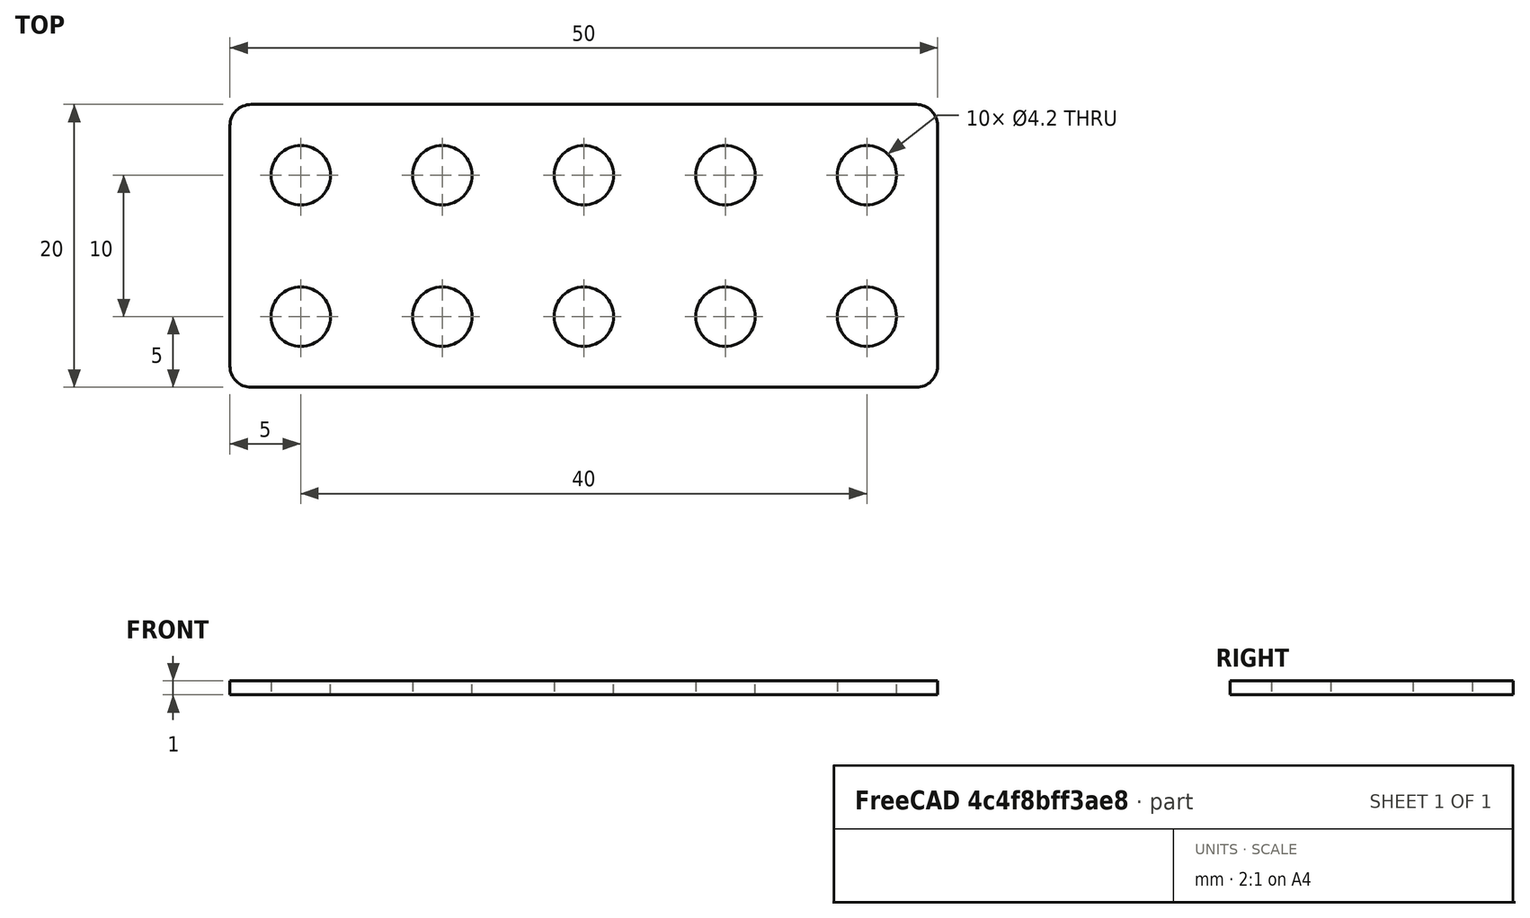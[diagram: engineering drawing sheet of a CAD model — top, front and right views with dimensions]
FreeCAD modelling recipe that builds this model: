
FCSTD DOCUMENT  (FreeCAD 0.16RUnknown)
Label: strip_2x5
License: All rights reserved
LicenseURL: http://en.wikipedia.org/wiki/All_rights_reserved
objects: Sketcher::SketchObject×1, PartDesign::Pad×1
note: 3 computed .brp shape members not serialized (recipe doc carries the construction recipe); baked Part::Feature solids carry a one-line shape summary decoded from their .brp

FEATURE [Sketcher::SketchObject] Sketch
  sketch-geometry (26):
    g0: LineSegment StartX=-3.5 StartY=15 StartZ=0 EndX=43.5 EndY=15 EndZ=0
    g1: LineSegment StartX=45 StartY=13.5 StartZ=0 EndX=45 EndY=-3.5 EndZ=0
    g2: LineSegment StartX=43.5 StartY=-5 StartZ=0 EndX=-3.5 EndY=-5 EndZ=0
    g3: LineSegment StartX=-5 StartY=-3.5 StartZ=0 EndX=-5 EndY=13.5 EndZ=0
    g4: ArcOfCircle CenterX=43.5 CenterY=13.5 CenterZ=0 NormalX=0 NormalY=0 NormalZ=1 Radius=1.5 StartAngle=0 EndAngle=1.5708
    g5: ArcOfCircle CenterX=43.5 CenterY=-3.5 CenterZ=0 NormalX=0 NormalY=0 NormalZ=1 Radius=1.5 StartAngle=4.71239 EndAngle=6.28319
    g6: ArcOfCircle CenterX=-3.5 CenterY=-3.5 CenterZ=0 NormalX=0 NormalY=0 NormalZ=1 Radius=1.5 StartAngle=3.14159 EndAngle=4.71239
    g7: ArcOfCircle CenterX=-3.5 CenterY=13.5 CenterZ=0 NormalX=0 NormalY=0 NormalZ=1 Radius=1.5 StartAngle=1.5708 EndAngle=3.14159
    g8: Circle CenterX=0 CenterY=0 CenterZ=0 NormalX=0 NormalY=0 NormalZ=1 Radius=2.1
    g9: Circle CenterX=0 CenterY=10 CenterZ=0 NormalX=0 NormalY=0 NormalZ=1 Radius=2.1
    g10: Circle CenterX=10 CenterY=0 CenterZ=0 NormalX=0 NormalY=0 NormalZ=1 Radius=2.1
    g11: LineSegment [constr] StartX=0 StartY=0 StartZ=0 EndX=10 EndY=0 EndZ=0
    g12: Circle CenterX=20 CenterY=0 CenterZ=0 NormalX=0 NormalY=0 NormalZ=1 Radius=2.1
    g13: LineSegment [constr] StartX=10 StartY=0 StartZ=0 EndX=20 EndY=0 EndZ=0
    g14: Circle CenterX=30 CenterY=0 CenterZ=0 NormalX=0 NormalY=0 NormalZ=1 Radius=2.1
    g15: LineSegment [constr] StartX=20 StartY=0 StartZ=0 EndX=30 EndY=0 EndZ=0
    g16: Circle CenterX=40 CenterY=0 CenterZ=0 NormalX=0 NormalY=0 NormalZ=1 Radius=2.1
    g17: LineSegment [constr] StartX=30 StartY=0 StartZ=0 EndX=40 EndY=0 EndZ=0
    g18: Circle CenterX=10 CenterY=10 CenterZ=0 NormalX=0 NormalY=0 NormalZ=1 Radius=2.1
    g19: LineSegment [constr] StartX=0 StartY=10 StartZ=0 EndX=10 EndY=10 EndZ=0
    g20: Circle CenterX=20 CenterY=10 CenterZ=0 NormalX=0 NormalY=0 NormalZ=1 Radius=2.1
    g21: LineSegment [constr] StartX=10 StartY=10 StartZ=0 EndX=20 EndY=10 EndZ=0
    g22: Circle CenterX=30 CenterY=10 CenterZ=0 NormalX=0 NormalY=0 NormalZ=1 Radius=2.1
    g23: LineSegment [constr] StartX=20 StartY=10 StartZ=0 EndX=30 EndY=10 EndZ=0
    g24: Circle CenterX=40 CenterY=10 CenterZ=0 NormalX=0 NormalY=0 NormalZ=1 Radius=2.1
    g25: LineSegment [constr] StartX=30 StartY=10 StartZ=0 EndX=40 EndY=10 EndZ=0
  constraints (65):
    c: Horizontal(g0)
    c: Horizontal(g2)
    c: Vertical(g1)
    c: Vertical(g3)
    c: Tangent(g0,g4) = 1.5708
    c: Tangent(g1,g4) = 1.5708
    c: Tangent(g1,g5) = 1.5708
    c: Tangent(g2,g5) = 1.5708
    c: Tangent(g3,g6) = 1.5708
    c: Tangent(g2,g6) = 1.5708
    c: Tangent(g3,g7) = 1.5708
    c: Tangent(g0,g7) = 1.5708
    c: Radius(g7) = 1.5
    c: Equal(g7,g4)
    c: Equal(g7,g5)
    c: Equal(g7,g6)
    c: Coincident(g8,g-1)
    c: Radius(g8) = 2.1
    c: Equal(g8,g9)
    c: DistanceY(g-1,g9) = 10
    c: DistanceX(g-1,g9) = 0
    c: Equal(g8,g10) = 2.1
    c: Coincident(g8,g11)
    c: Coincident(g10,g11)
    c: Distance(g11) = 10
    c: Angle(g11) = 0
    c: Equal(g8,g12) = 2.1
    c: Coincident(g10,g13)
    c: Coincident(g12,g13)
    c: Equal(g11,g13)
    c: Parallel(g13,g11)
    c: Equal(g8,g14) = 2.1
    c: Coincident(g12,g15)
    c: Coincident(g14,g15)
    c: Equal(g11,g15)
    c: Parallel(g15,g11)
    c: Equal(g8,g16) = 2.1
    c: Coincident(g14,g17)
    c: Coincident(g16,g17)
    c: Equal(g11,g17)
    c: Parallel(g17,g11)
    c: Coincident(g9,g19)
    c: Coincident(g18,g19)
    c: Distance(g19) = 10
    c: Angle(g19) = 0
    c: Coincident(g18,g21)
    c: Coincident(g20,g21)
    c: Equal(g19,g21)
    c: Parallel(g21,g19)
    c: Coincident(g20,g23)
    c: Coincident(g22,g23)
    c: Equal(g19,g23)
    c: Parallel(g23,g19)
    c: Coincident(g22,g25)
    c: Coincident(g24,g25)
    c: Equal(g19,g25)
    c: Parallel(g25,g19)
    c: Equal(g8,g18)
    c: Equal(g8,g20)
    c: Equal(g8,g22)
    c: Equal(g8,g24)
    c: DistanceX(g3,g9) = 5
    c: DistanceY(g9,g0) = 5
    c: DistanceY(g2,g16) = 5
    c: DistanceX(g16,g1) = 5
FEATURE [PartDesign::Pad] Pad
  Length = 1
  Length2 = 100
  Sketch = -> Sketch
  Type = 0
